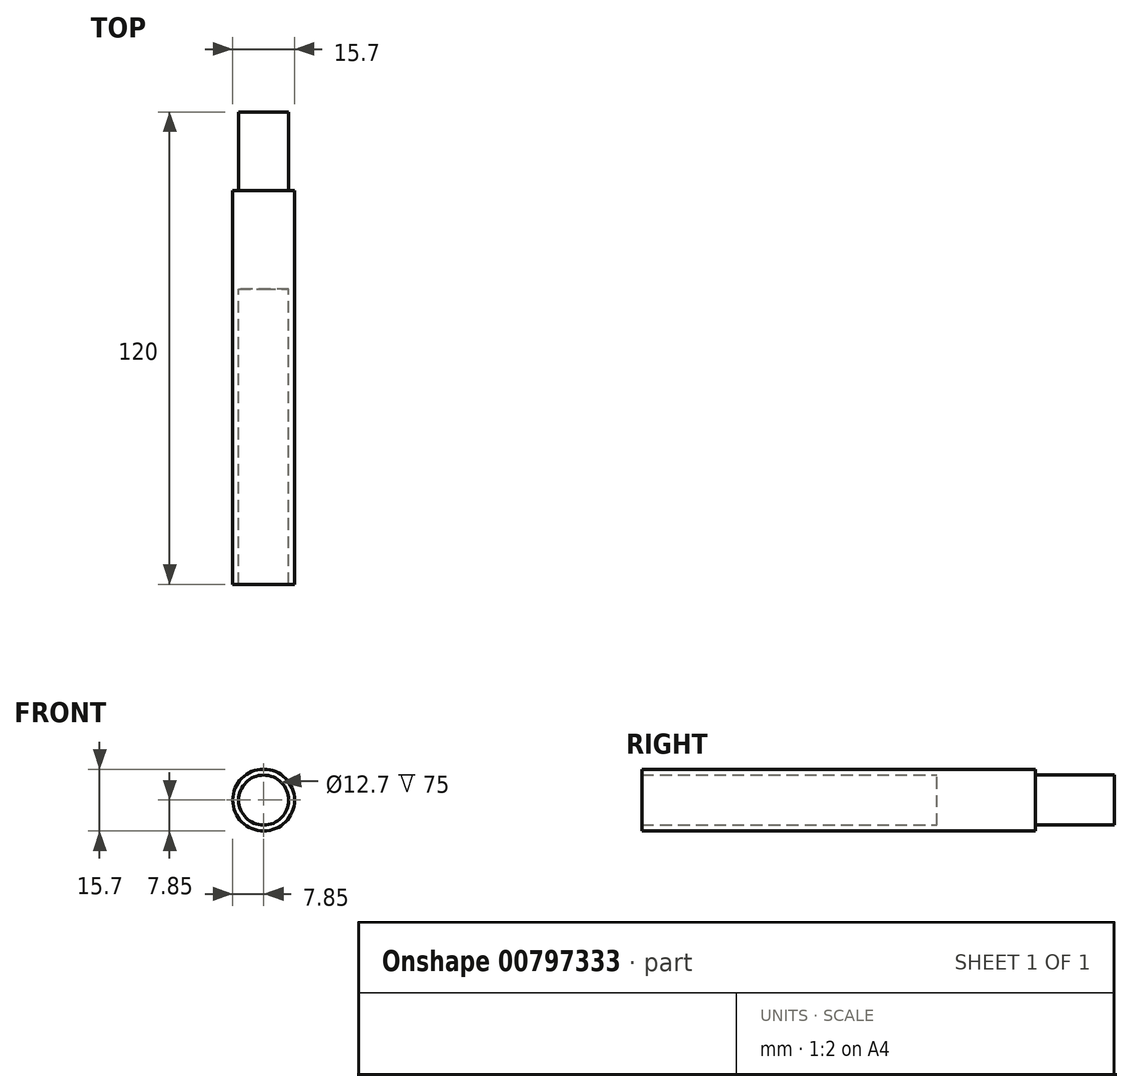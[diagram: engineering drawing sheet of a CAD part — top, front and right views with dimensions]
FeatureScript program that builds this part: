
annotation { "Feature Type Name" : "Feature", "Feature Type Description" : "" }
export const myFeature = defineFeature(function(context is Context, id is Id, definition is map)
    precondition{}
    {
        {
            var Q0;
            Q0=qCreatedBy(makeId("Front.planeOp"),FACE);
            var sketch = newSketch(context, id + "F0", { "sketchPlane" : qUnion([Q0])});
            skCircle(sketch, "E0", {"center": v(0, 0) * mm, "radius": 6.35 * mm});
            skCircle(sketch, "E1", {"center": v(0, 0) * mm, "radius": 7.85 * mm});
            skSolve(sketch);
        }
        {
            var Q0;
            Q0 = qSketchRegion(id + "F0", true);
            extrude(context, id + "F1", {"entities" : qUnion([Q0]), "depth" : 100 * mm, "offsetDistance" : 25 * mm});
        }
        {
            var Q0;
            Q0=makeQuery(id+"F0.imprint","IMPRINT",FACE,{"disambiguationData":[TD([[makeQuery(id+"F0.imprint","IMPRINT",EDGE,{"derivedFrom":sQuery(id+"F0.wireOp",EDGE,"E0")}),1.0]])]});
            extrude(context, id + "F2", {"entities" : qUnion([Q0]), "operationType" : NewBodyOperationType.ADD, "depth" : 25 * mm, "offsetDistance" : 25 * mm, "hasSecondDirection" : true, "secondDirectionOppositeDirection" : true, "secondDirectionDepth" : 20 * mm});
        }
    });
